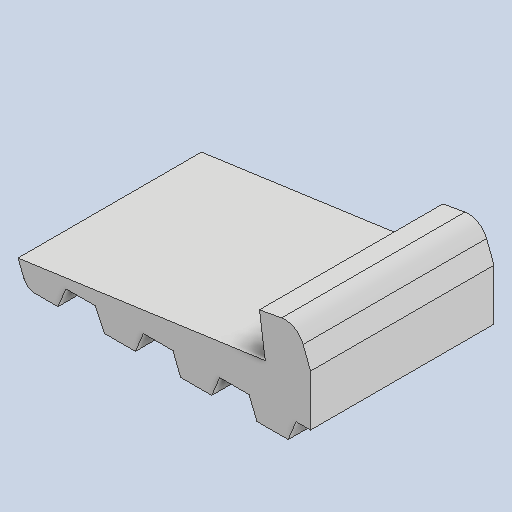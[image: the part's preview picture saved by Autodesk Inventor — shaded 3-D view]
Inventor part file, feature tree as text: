
AUTODESK INVENTOR PART (.ipt)
format: ipt  version: 2022 (Build 260153000, 153)  size: 96,768 bytes
history: native  units: in
note: dims shown in document units (in); Inventor stores cm internally (conversion verified against a paired STEP export)
features: extrude x1
ambient origin geometry x8: Origin, YZ Plane, XZ Plane, XY Plane, X Axis, Y Axis, Z Axis, Center Point
bodies: Solid1 (feature_tree)
feature tree (1):
  extrude  "Extrusion1"  [1 undecoded]
note: 1 required parameter value undecoded (feature->parameter linkage not recoverable at this tier; creation-order binding heuristic only, values carry confidence <= 0.55)
